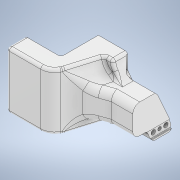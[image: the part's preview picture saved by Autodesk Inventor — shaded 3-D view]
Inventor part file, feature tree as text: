
AUTODESK INVENTOR PART (.ipt)
format: ipt  version: 2020 (Build 240168000, 168)  size: 688,640 bytes
history: native  units: in
note: dims shown in document units (in); Inventor stores cm internally (conversion verified against a paired STEP export)
features: fillet x22, sketch x11, extrude x9, projected_geometry x3, plane x2, other x1
ambient origin geometry x8: Origin, YZ Plane, XZ Plane, XY Plane, X Axis, Y Axis, Z Axis, Center Point
bodies: Solid1 (feature_tree)
feature tree (48):
  extrude  "Extrusion1"  Depth=0.3937in TaperAngle=0.0deg
  extrude  "Extrusion2"  Depth=0.0394in TaperAngle=0.0deg
  fillet  "Fillet1"  Radius=0.0394in
  extrude  "Extrusion4"  Depth=0.3937in
  fillet  "Fillet2"  [1 undecoded]
  sketch  "Sketch9"  dims[d25=0.3937in d26=0.0in d27=0.3937in d30=0.1181in d31=0.2165in]
  extrude  "Extrusion8"  Depth=0.3937in
  fillet  "Fillet3"  Radius=0.1181in
  fillet  "Fillet6"  Radius=0.2165in
  extrude  "Extrusion9"  Depth=0.7087in
  extrude  "Extrusion11"  Depth=1.063in
  extrude  "Extrusion12"  Depth=0.3937in
  fillet  "Fillet7"  Radius=0.7087in
  fillet  "Fillet8"  Radius=0.7087in
  fillet  "Fillet9"  Radius=0.3937in
  fillet  "Fillet10"  Radius=0.3937in
  fillet  "Fillet11"  Radius=0.3937in
  fillet  "Fillet12"  Radius=0.5906in
  fillet  "Fillet13"  Radius=0.1969in
  fillet  "Fillet14"  Radius=0.0787in
  fillet  "Fillet15"  Radius=0.0787in
  fillet  "Fillet16"  Radius=0.0787in
  fillet  "Fillet17"  Radius=0.0787in
  fillet  "Fillet19"  Radius=0.0787in
  plane  "Work Plane1"
  plane  "Work Plane2"
  extrude  "Extrusion14"  Depth=0.0787in
  fillet  "Fillet20"  [1 undecoded]
  sketch  "Sketch18"  dims[d71=0.0079in]
  extrude  "Extrusion15"  Depth=0.0079in TaperAngle=0.0deg
  fillet  "Fillet21"  Radius=0.0787in
  fillet  "Fillet22"  Radius=0.0266in
  fillet  "Fillet23"  Radius=0.0079in
  fillet  "Fillet24"  Radius=0.0079in
  fillet  "Fillet25"  Radius=0.0079in
  sketch  "Sketch1"  dims[d0=0.3937in d1=0.0in d6=0.3937in d7=0.0in]
  sketch  "Sketch3"  dims[d10=0.0394in d11=0.0984in d12=0.0in d21=0.0394in]
  sketch  "Sketch5"  dims[d22=0.3937in d23=0.3937in d24=0.0in]
  projected_geometry  "Projected Loop1"
  sketch  "Sketch10"  dims[d32=0.2165in d33=0.7087in]
  sketch  "Sketch11"  dims[d34=0.7087in d35=0.0in d38=1.063in]
  sketch  "Sketch13"  dims[d40=0.5118in d41=1.0236in d42=0.7087in d43=0.0in d44=0.7087in d45=0.0in d46=0.3937in d47=0.3937in d48=0.3937in d49=0.5906in d50=0.1969in d51=0.0787in d52=0.0787in d53=0.0787in d54=0.0787in d55=0.0787in]
  sketch  "Sketch14"  dims[d56=0.1969in d58=0.0787in d59=-0.0787in]
  projected_geometry  "Projected Loop4"
  sketch  "Sketch17"  dims[d62=0.0899in d63=0.2859in d64=0.0in d65=0.0787in d66=0.0266in d67=0.0in d68=0.0079in d69=0.0079in d70=0.0079in]
  projected_geometry  "Projected Loop5"
  sketch  "Sketch19"  dims[d72=0.0079in d2=0.0197in d3=1.9685in]
  other  "Trous de centrage Ø2.0mm1"
note: 2 required parameter values undecoded (feature->parameter linkage not recoverable at this tier; creation-order binding heuristic only, values carry confidence <= 0.55)
